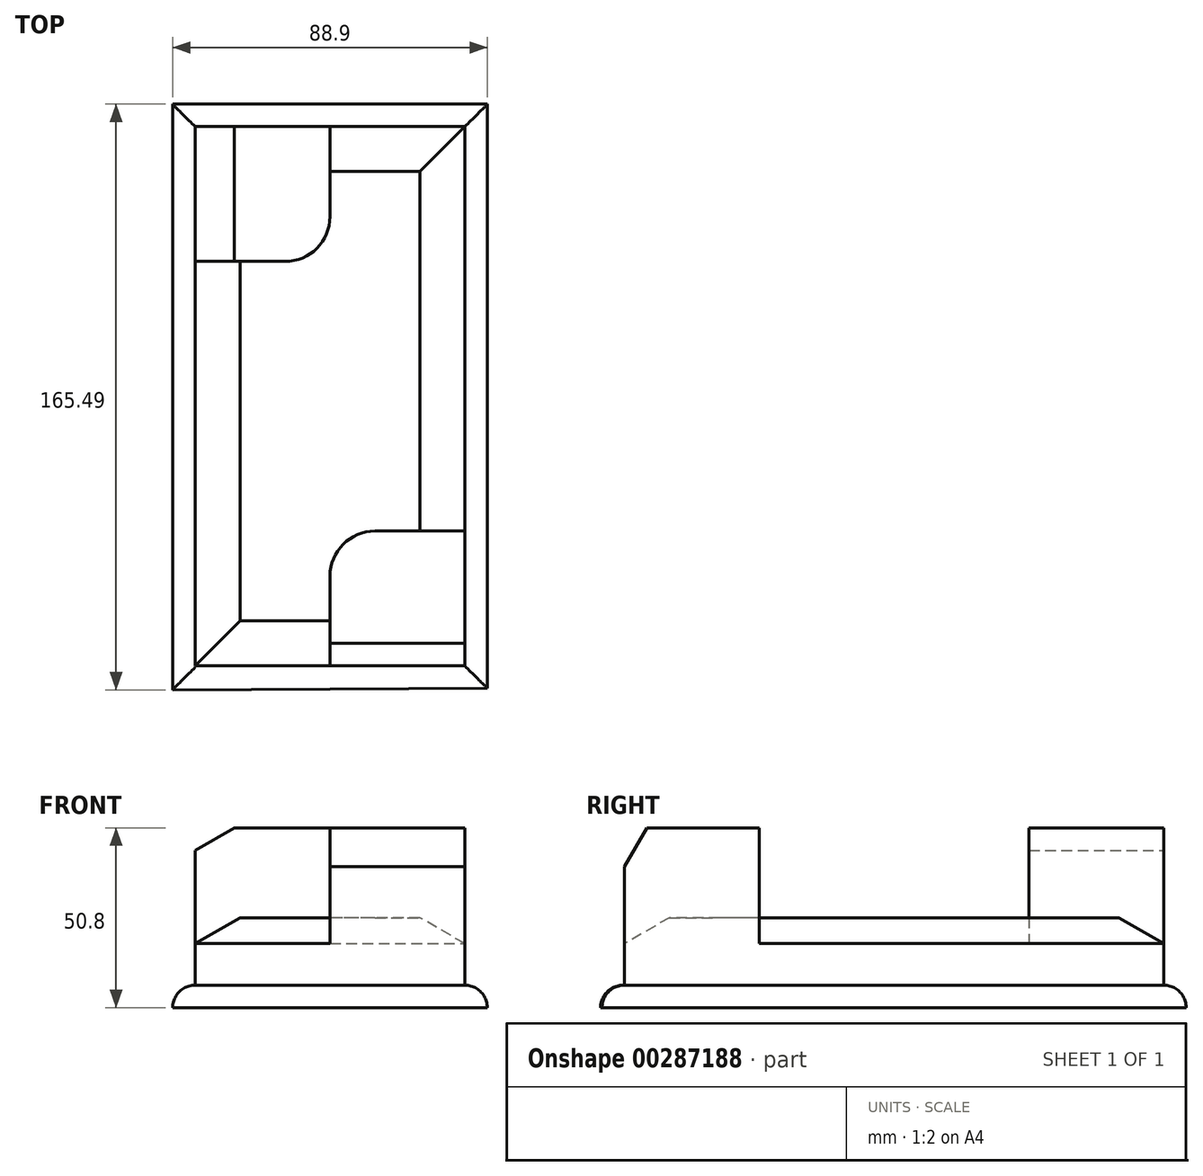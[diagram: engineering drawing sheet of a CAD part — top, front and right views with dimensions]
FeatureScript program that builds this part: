
annotation { "Feature Type Name" : "Feature", "Feature Type Description" : "" }
export const myFeature = defineFeature(function(context is Context, id is Id, definition is map)
    precondition{}
    {
        {
            var Q0;
            Q0=qCreatedBy(makeId("Top.planeOp"),FACE);
            var sketch = newSketch(context, id + "F0", { "sketchPlane" : qUnion([Q0])});
            skLineSegment(sketch, "E0.bottom", {"start": v(-43.83, -90.78) * mm, "end": v(32.37, -90.78) * mm});
            skLineSegment(sketch, "E0.top", {"start": v(-43.83, 61.62) * mm, "end": v(32.37, 61.62) * mm});
            skLineSegment(sketch, "E0.left", {"start": v(-43.83, -90.78) * mm, "end": v(-43.83, 61.62) * mm});
            skLineSegment(sketch, "E0.right", {"start": v(32.37, -90.78) * mm, "end": v(32.37, 61.62) * mm});
            skLineSegment(sketch, "E1", {"start": v(-50.18, -97.52) * mm, "end": v(-50.18, 67.97) * mm});
            skLineSegment(sketch, "E2", {"start": v(-50.18, 67.97) * mm, "end": v(38.72, 67.97) * mm});
            skLineSegment(sketch, "E3", {"start": v(38.72, 67.97) * mm, "end": v(38.72, -97.1) * mm});
            skLineSegment(sketch, "E4", {"start": v(38.72, -97.1) * mm, "end": v(-50.18, -97.52) * mm});
            skLineSegment(sketch, "E5", {"start": v(-5.73, -90.78) * mm, "end": v(-5.73, -65.38) * mm});
            skLineSegment(sketch, "E6", {"start": v(6.97, -52.68) * mm, "end": v(32.37, -52.68) * mm});
            skLineSegment(sketch, "E7", {"start": v(-5.73, 61.62) * mm, "end": v(-5.73, 36.22) * mm});
            skLineSegment(sketch, "E8", {"start": v(-18.43, 23.52) * mm, "end": v(-43.83, 23.52) * mm});
            skPoint(sketch, "E9.visualSharp", {"position": v(-5.73, 23.52) * mm});
            skArc(sketch, "E9.filletArc", {"start": v(-18.43, 23.52) * mm, "mid": v(-9.45, 27.24) * mm, "end": v(-5.73, 36.22) * mm});
            skPoint(sketch, "E10.visualSharp", {"position": v(-5.73, -52.68) * mm});
            skArc(sketch, "E10.filletArc", {"start": v(6.97, -52.68) * mm, "mid": v(-2.01, -56.4) * mm, "end": v(-5.73, -65.38) * mm});
            skSolve(sketch);
        }
        {
            var Q0;
            Q0=makeQuery(id+"F0.imprint","IMPRINT",FACE,{"disambiguationData":[TD([[makeQuery(id+"F0.imprint","IMPRINT",EDGE,{"derivedFrom":sQuery(id+"F0.wireOp",EDGE,"E1")}),-1.0]])]});
            extrude(context, id + "F1", {"entities" : qUnion([Q0]), "depth" : 6.35 * mm});
        }
        {
            var Q0;
            {var subQ9=sQuery(id+"F0.wireOp",EDGE,"E5");Q0=makeQuery(id+"F0.imprint","IMPRINT",FACE,{"disambiguationData":[TD([[makeQuery(id+"F0.imprint","IMPRINT",EDGE,{"derivedFrom":subQ9}),1.0]])]});}
            extrude(context, id + "F2", {"entities" : qUnion([Q0]), "operationType" : NewBodyOperationType.ADD, "depth" : 25.4 * mm});
        }
        {
            var Q0;
            {var subQ0=sQuery(id+"F0.wireOp",EDGE,"E7");Q0=makeQuery(id+"F0.imprint","IMPRINT",FACE,{"disambiguationData":[TD([[makeQuery(id+"F0.imprint","IMPRINT",EDGE,{"derivedFrom":subQ0}),-1.0]])]});}
            var Q1;
            {var subQ1=sQuery(id+"F0.wireOp",EDGE,"E5");Q1=makeQuery(id+"F0.imprint","IMPRINT",FACE,{"disambiguationData":[TD([[makeQuery(id+"F0.imprint","IMPRINT",EDGE,{"derivedFrom":subQ1}),-1.0]])]});}
            extrude(context, id + "F3", {"entities" : qUnion([Q0, Q1]), "operationType" : NewBodyOperationType.ADD, "depth" : 50.8 * mm});
        }
        {
            var Q0;
            Q0=makeQuery(id+"F3.opExtrude","CAP_EDGE",EDGE,{"disambiguationData":[OSD([sQuery(id+"F0.wireOp",EDGE,"E0.bottom")])],"isStart":false});
            var Q1;
            Q1=makeQuery(id+"F3.opExtrude","CAP_EDGE",EDGE,{"disambiguationData":[OSD([sQuery(id+"F0.wireOp",EDGE,"E0.left")])],"isStart":false});
            chamfer(context, id + "F4", {"entities" : qUnion([Q0, Q1]), "chamferType" : ChamferType.OFFSET_ANGLE, "width" : 6.35 * mm, "oppositeDirection" : false, "angle" : 60 * degree, "tangentPropagation" : true});
        }
        {
            var Q0;
            Q0=makeQuery(id+"F2.opExtrude","CAP_EDGE",EDGE,{"disambiguationData":[OSD([sQuery(id+"F0.wireOp",EDGE,"E0.right")])],"isStart":false});
            var Q1;
            Q1=makeQuery(id+"F2.opExtrude","CAP_EDGE",EDGE,{"disambiguationData":[OSD([sQuery(id+"F0.wireOp",EDGE,"E0.bottom")])],"isStart":false});
            var Q2;
            Q2=makeQuery(id+"F2.opExtrude","CAP_EDGE",EDGE,{"disambiguationData":[OSD([sQuery(id+"F0.wireOp",EDGE,"E0.left")])],"isStart":false});
            var Q3;
            Q3=makeQuery(id+"F2.opExtrude","CAP_EDGE",EDGE,{"disambiguationData":[OSD([sQuery(id+"F0.wireOp",EDGE,"E0.top")])],"isStart":false});
            chamfer(context, id + "F5", {"entities" : qUnion([Q0, Q1, Q2, Q3]), "chamferType" : ChamferType.OFFSET_ANGLE, "width" : 12.7 * mm, "oppositeDirection" : false, "angle" : 30 * degree, "tangentPropagation" : true});
        }
        {
            var Q0;
            Q0=makeQuery(id+"F1.opExtrude","CAP_EDGE",EDGE,{"disambiguationData":[OSD([sQuery(id+"F0.wireOp",EDGE,"E3")])],"isStart":false});
            var Q1;
            Q1=makeQuery(id+"F1.opExtrude","CAP_EDGE",EDGE,{"disambiguationData":[OSD([sQuery(id+"F0.wireOp",EDGE,"E4")])],"isStart":false});
            var Q2;
            Q2=makeQuery(id+"F1.opExtrude","CAP_EDGE",EDGE,{"disambiguationData":[OSD([sQuery(id+"F0.wireOp",EDGE,"E2")])],"isStart":false});
            var Q3;
            Q3=makeQuery(id+"F1.opExtrude","CAP_EDGE",EDGE,{"disambiguationData":[OSD([sQuery(id+"F0.wireOp",EDGE,"E1")])],"isStart":false});
            fillet(context, id + "F6", {"entities" : qUnion([Q0, Q1, Q2, Q3]), "radius" : 6.35 * mm, "tangentPropagation" : true, "allowEdgeOverflow" : false});
        }
    });
